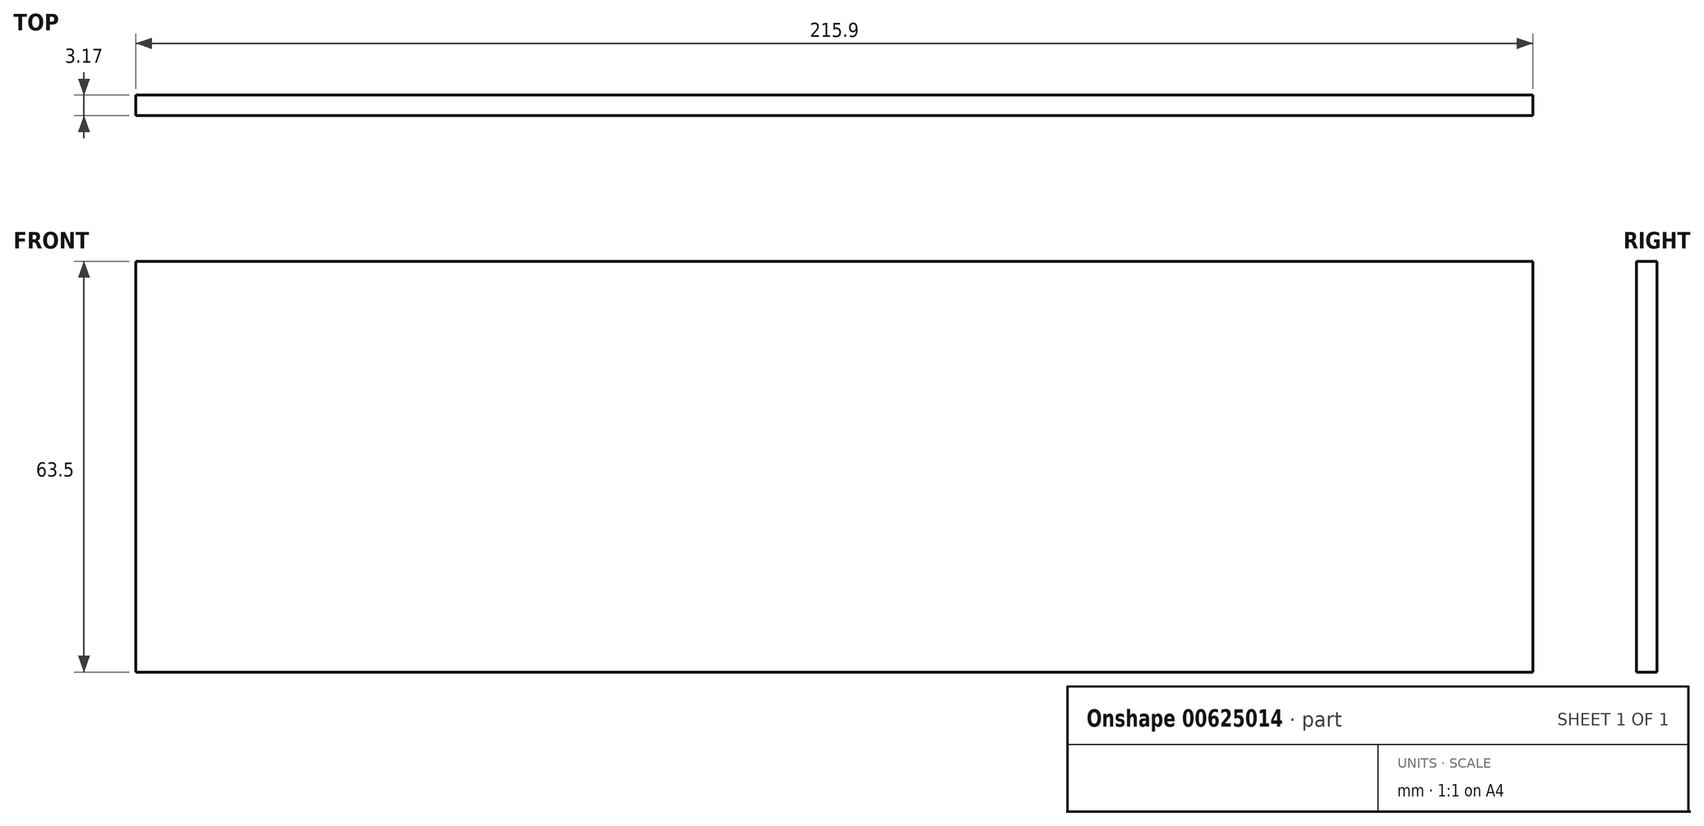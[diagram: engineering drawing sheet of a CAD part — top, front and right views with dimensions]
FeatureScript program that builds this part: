
annotation { "Feature Type Name" : "Feature", "Feature Type Description" : "" }
export const myFeature = defineFeature(function(context is Context, id is Id, definition is map)
    precondition{}
    {
        {
            var Q0;
            Q0=qCreatedBy(makeId("Front.planeOp"),FACE);
            var sketch = newSketch(context, id + "F0", { "sketchPlane" : qUnion([Q0])});
            skLineSegment(sketch, "E0.bottom", {"start": v(0, 0) * mm, "end": v(215.9, 0) * mm});
            skLineSegment(sketch, "E0.top", {"start": v(0, 63.5) * mm, "end": v(215.9, 63.5) * mm});
            skLineSegment(sketch, "E0.left", {"start": v(0, 0) * mm, "end": v(0, 63.5) * mm});
            skLineSegment(sketch, "E0.right", {"start": v(215.9, 0) * mm, "end": v(215.9, 63.5) * mm});
            skSolve(sketch);
        }
        {
            var Q0;
            Q0=makeQuery(id+"F0.imprint","IMPRINT",FACE,{"disambiguationData":[TD([[makeQuery(id+"F0.imprint","IMPRINT",EDGE,{"derivedFrom":sQuery(id+"F0.wireOp",EDGE,"E0.bottom")}),1.0]])]});
            extrude(context, id + "F1", {"entities" : qUnion([Q0]), "depth" : 3.17 * mm, "offsetDistance" : 25.4 * mm});
        }
    });
